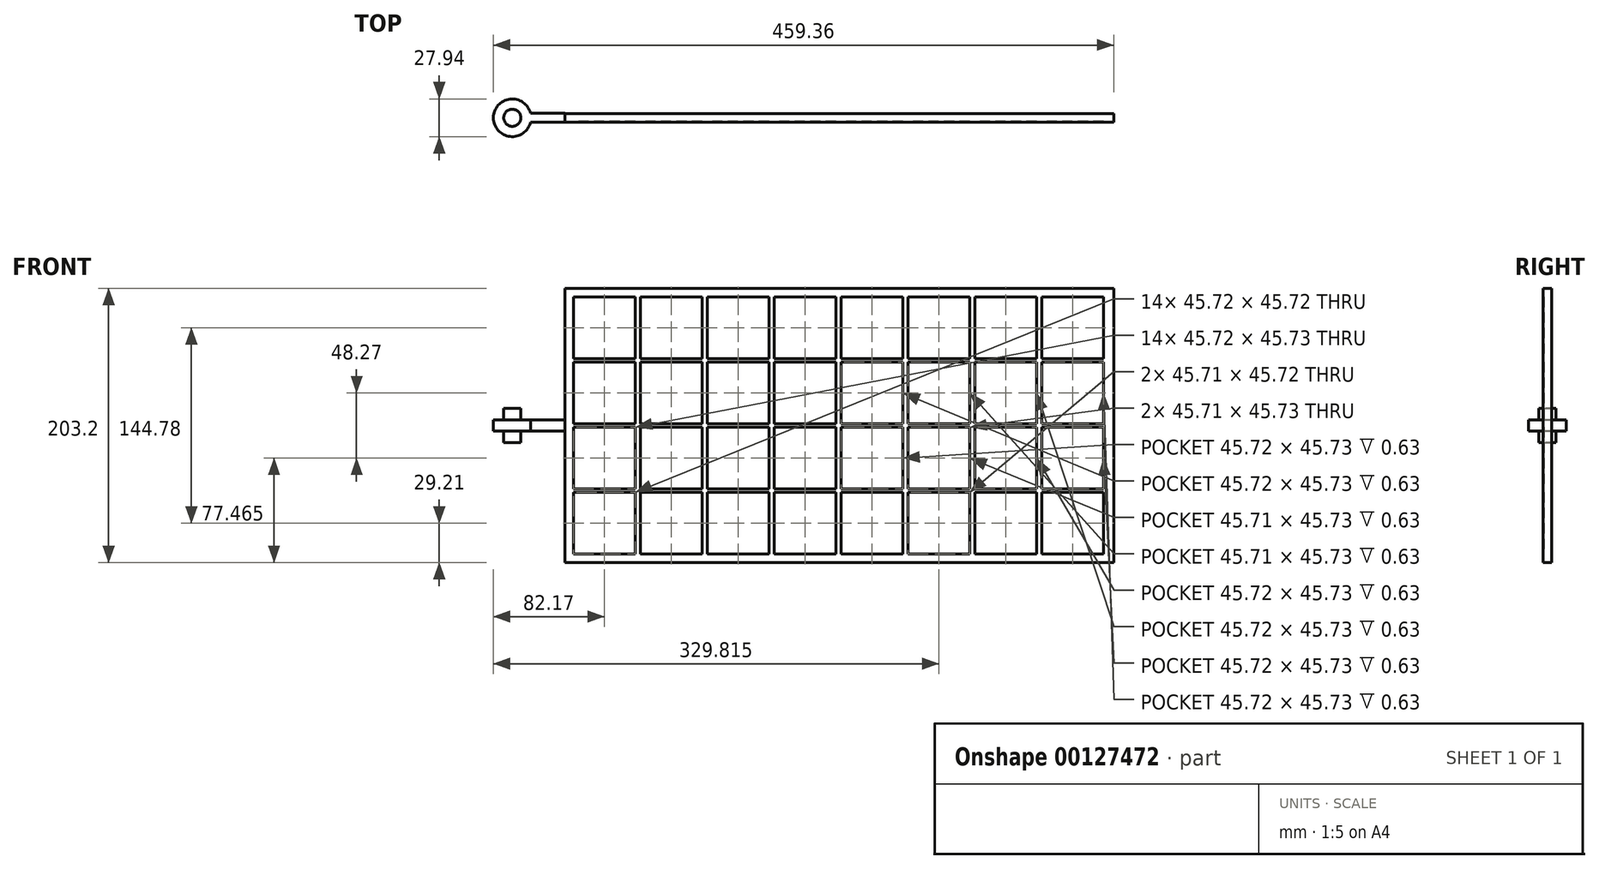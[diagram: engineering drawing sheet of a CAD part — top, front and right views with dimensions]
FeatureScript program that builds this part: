
annotation { "Feature Type Name" : "Feature", "Feature Type Description" : "" }
export const myFeature = defineFeature(function(context is Context, id is Id, definition is map)
    precondition{}
    {
        {
            var Q0;
            Q0=qCreatedBy(makeId("Top.planeOp"),FACE);
            var sketch = newSketch(context, id + "F0", { "sketchPlane" : qUnion([Q0])});
            skCircle(sketch, "E0", {"center": v(0, 0) * mm, "radius": 6.35 * mm});
            skSolve(sketch);
        }
        {
            var Q0;
            Q0 = qSketchRegion(id + "F0", true);
            extrude(context, id + "F1", {"entities" : qUnion([Q0]), "endBound" : BoundingType.SYMMETRIC, "depth" : 25.4 * mm});
        }
        {
            var Q0;
            Q0=qCreatedBy(makeId("Top.planeOp"),FACE);
            var sketch = newSketch(context, id + "F2", { "sketchPlane" : qUnion([Q0])});
            skArc(sketch, "E1", {"start": v(13.59, 3.26) * mm, "mid": v(-13.97, 0) * mm, "end": v(13.59, -3.26) * mm});
            skCircle(sketch, "E2.0", {"center": v(0, 0) * mm, "radius": 6.35 * mm});
            skLineSegment(sketch, "E3", {"start": v(13.59, 3.26) * mm, "end": v(38.99, 3.26) * mm});
            skLineSegment(sketch, "E4", {"start": v(0, 0) * mm, "end": v(2.18, 0) * mm});
            skLineSegment(sketch, "E5.MirrorCS", {"start": v(13.59, -3.26) * mm, "end": v(38.99, -3.26) * mm});
            skLineSegment(sketch, "E6", {"start": v(38.99, 3.26) * mm, "end": v(38.99, -3.26) * mm});
            skSolve(sketch);
        }
        {
            var Q0;
            Q0 = qSketchRegion(id + "F2", true);
            extrude(context, id + "F3", {"entities" : qUnion([Q0]), "operationType" : NewBodyOperationType.ADD, "endBound" : BoundingType.SYMMETRIC, "depth" : 8.38 * mm});
        }
        {
            var Q0;
            Q0=qCreatedBy(makeId("Front.planeOp"),FACE);
            var sketch = newSketch(context, id + "F4", { "sketchPlane" : qUnion([Q0])});
            skLineSegment(sketch, "E7.0", {"start": v(38.99, 4.2) * mm, "end": v(38.99, -4.2) * mm});
            skLineSegment(sketch, "E8", {"start": v(38.99, 0) * mm, "end": v(38.99, 101.6) * mm});
            skPoint(sketch, "E8.endSnap0", {"position": v(38.99, 0) * mm});
            skLineSegment(sketch, "E9", {"start": v(38.99, 0) * mm, "end": v(38.99, -101.6) * mm});
            skLineSegment(sketch, "E10", {"start": v(38.99, 101.6) * mm, "end": v(445.39, 101.6) * mm});
            skLineSegment(sketch, "E11.top", {"start": v(38.99, -101.6) * mm, "end": v(445.39, -101.6) * mm});
            skLineSegment(sketch, "E11.left", {"start": v(38.99, 101.6) * mm, "end": v(38.99, -101.6) * mm});
            skLineSegment(sketch, "E11.right", {"start": v(445.39, 101.6) * mm, "end": v(445.39, -101.6) * mm});
            skLineSegment(sketch, "E12.bottom", {"start": v(45.34, -95.25) * mm, "end": v(91.06, -95.25) * mm});
            skLineSegment(sketch, "E12.top", {"start": v(45.34, -49.53) * mm, "end": v(91.06, -49.53) * mm});
            skLineSegment(sketch, "E12.left", {"start": v(45.34, -95.25) * mm, "end": v(45.34, -49.53) * mm});
            skLineSegment(sketch, "E12.right", {"start": v(91.06, -95.25) * mm, "end": v(91.06, -49.53) * mm});
            skLineSegment(sketch, "E13.0.1.0", {"start": v(91.06, -47) * mm, "end": v(91.06, -1.27) * mm});
            skLineSegment(sketch, "E13.0.1.1", {"start": v(45.34, -47) * mm, "end": v(45.34, -1.27) * mm});
            skLineSegment(sketch, "E13.0.1.2", {"start": v(45.34, -1.27) * mm, "end": v(91.06, -1.27) * mm});
            skLineSegment(sketch, "E13.0.1.3", {"start": v(45.34, -47) * mm, "end": v(91.06, -47) * mm});
            skLineSegment(sketch, "E13.0.2.0", {"start": v(91.06, 1.27) * mm, "end": v(91.06, 47) * mm});
            skLineSegment(sketch, "E13.0.2.1", {"start": v(45.34, 1.27) * mm, "end": v(45.34, 47) * mm});
            skLineSegment(sketch, "E13.0.2.2", {"start": v(45.34, 47) * mm, "end": v(91.06, 47) * mm});
            skLineSegment(sketch, "E13.0.2.3", {"start": v(45.34, 1.27) * mm, "end": v(91.06, 1.27) * mm});
            skLineSegment(sketch, "E13.0.3.0", {"start": v(91.06, 49.53) * mm, "end": v(91.06, 95.25) * mm});
            skLineSegment(sketch, "E13.0.3.1", {"start": v(45.34, 49.53) * mm, "end": v(45.34, 95.25) * mm});
            skLineSegment(sketch, "E13.0.3.2", {"start": v(45.34, 95.25) * mm, "end": v(91.06, 95.25) * mm});
            skLineSegment(sketch, "E13.0.3.3", {"start": v(45.34, 49.53) * mm, "end": v(91.06, 49.53) * mm});
            skLineSegment(sketch, "E13.1.0.0", {"start": v(140.59, -95.25) * mm, "end": v(140.59, -49.53) * mm});
            skLineSegment(sketch, "E13.1.0.1", {"start": v(94.87, -95.25) * mm, "end": v(94.87, -49.53) * mm});
            skLineSegment(sketch, "E13.1.0.2", {"start": v(94.87, -49.53) * mm, "end": v(140.59, -49.53) * mm});
            skLineSegment(sketch, "E13.1.0.3", {"start": v(94.87, -95.25) * mm, "end": v(140.59, -95.25) * mm});
            skLineSegment(sketch, "E13.1.1.0", {"start": v(140.59, -47) * mm, "end": v(140.59, -1.27) * mm});
            skLineSegment(sketch, "E13.1.1.1", {"start": v(94.87, -47) * mm, "end": v(94.87, -1.27) * mm});
            skLineSegment(sketch, "E13.1.1.2", {"start": v(94.87, -1.27) * mm, "end": v(140.59, -1.27) * mm});
            skLineSegment(sketch, "E13.1.1.3", {"start": v(94.87, -47) * mm, "end": v(140.59, -47) * mm});
            skLineSegment(sketch, "E13.1.2.0", {"start": v(140.59, 1.27) * mm, "end": v(140.59, 47) * mm});
            skLineSegment(sketch, "E13.1.2.1", {"start": v(94.87, 1.27) * mm, "end": v(94.87, 47) * mm});
            skLineSegment(sketch, "E13.1.2.2", {"start": v(94.87, 47) * mm, "end": v(140.59, 47) * mm});
            skLineSegment(sketch, "E13.1.2.3", {"start": v(94.87, 1.27) * mm, "end": v(140.59, 1.27) * mm});
            skLineSegment(sketch, "E13.1.3.0", {"start": v(140.59, 49.53) * mm, "end": v(140.59, 95.25) * mm});
            skLineSegment(sketch, "E13.1.3.1", {"start": v(94.87, 49.53) * mm, "end": v(94.87, 95.25) * mm});
            skLineSegment(sketch, "E13.1.3.2", {"start": v(94.87, 95.25) * mm, "end": v(140.59, 95.25) * mm});
            skLineSegment(sketch, "E13.1.3.3", {"start": v(94.87, 49.53) * mm, "end": v(140.59, 49.53) * mm});
            skLineSegment(sketch, "E13.2.0.0", {"start": v(190.12, -95.25) * mm, "end": v(190.12, -49.53) * mm});
            skLineSegment(sketch, "E13.2.0.1", {"start": v(144.4, -95.25) * mm, "end": v(144.4, -49.53) * mm});
            skLineSegment(sketch, "E13.2.0.2", {"start": v(144.4, -49.53) * mm, "end": v(190.12, -49.53) * mm});
            skLineSegment(sketch, "E13.2.0.3", {"start": v(144.4, -95.25) * mm, "end": v(190.12, -95.25) * mm});
            skLineSegment(sketch, "E13.2.1.0", {"start": v(190.12, -47) * mm, "end": v(190.12, -1.27) * mm});
            skLineSegment(sketch, "E13.2.1.1", {"start": v(144.4, -47) * mm, "end": v(144.4, -1.27) * mm});
            skLineSegment(sketch, "E13.2.1.2", {"start": v(144.4, -1.27) * mm, "end": v(190.12, -1.27) * mm});
            skLineSegment(sketch, "E13.2.1.3", {"start": v(144.4, -47) * mm, "end": v(190.12, -47) * mm});
            skLineSegment(sketch, "E13.2.2.0", {"start": v(190.12, 1.27) * mm, "end": v(190.12, 47) * mm});
            skLineSegment(sketch, "E13.2.2.1", {"start": v(144.4, 1.27) * mm, "end": v(144.4, 47) * mm});
            skLineSegment(sketch, "E13.2.2.2", {"start": v(144.4, 47) * mm, "end": v(190.12, 47) * mm});
            skLineSegment(sketch, "E13.2.2.3", {"start": v(144.4, 1.27) * mm, "end": v(190.12, 1.27) * mm});
            skLineSegment(sketch, "E13.2.3.0", {"start": v(190.12, 49.53) * mm, "end": v(190.12, 95.25) * mm});
            skLineSegment(sketch, "E13.2.3.1", {"start": v(144.4, 49.53) * mm, "end": v(144.4, 95.25) * mm});
            skLineSegment(sketch, "E13.2.3.2", {"start": v(144.4, 95.25) * mm, "end": v(190.12, 95.25) * mm});
            skLineSegment(sketch, "E13.2.3.3", {"start": v(144.4, 49.53) * mm, "end": v(190.12, 49.53) * mm});
            skLineSegment(sketch, "E13.3.0.0", {"start": v(239.65, -95.25) * mm, "end": v(239.65, -49.53) * mm});
            skLineSegment(sketch, "E13.3.0.1", {"start": v(193.93, -95.25) * mm, "end": v(193.93, -49.53) * mm});
            skLineSegment(sketch, "E13.3.0.2", {"start": v(193.93, -49.53) * mm, "end": v(239.65, -49.53) * mm});
            skLineSegment(sketch, "E13.3.0.3", {"start": v(193.93, -95.25) * mm, "end": v(239.65, -95.25) * mm});
            skLineSegment(sketch, "E13.3.1.0", {"start": v(239.65, -47) * mm, "end": v(239.65, -1.27) * mm});
            skLineSegment(sketch, "E13.3.1.1", {"start": v(193.93, -47) * mm, "end": v(193.93, -1.27) * mm});
            skLineSegment(sketch, "E13.3.1.2", {"start": v(193.93, -1.27) * mm, "end": v(239.65, -1.27) * mm});
            skLineSegment(sketch, "E13.3.1.3", {"start": v(193.93, -47) * mm, "end": v(239.65, -47) * mm});
            skLineSegment(sketch, "E13.3.2.0", {"start": v(239.65, 1.27) * mm, "end": v(239.65, 47) * mm});
            skLineSegment(sketch, "E13.3.2.1", {"start": v(193.93, 1.27) * mm, "end": v(193.93, 47) * mm});
            skLineSegment(sketch, "E13.3.2.2", {"start": v(193.93, 47) * mm, "end": v(239.65, 47) * mm});
            skLineSegment(sketch, "E13.3.2.3", {"start": v(193.93, 1.27) * mm, "end": v(239.65, 1.27) * mm});
            skLineSegment(sketch, "E13.3.3.0", {"start": v(239.65, 49.53) * mm, "end": v(239.65, 95.25) * mm});
            skLineSegment(sketch, "E13.3.3.1", {"start": v(193.93, 49.53) * mm, "end": v(193.93, 95.25) * mm});
            skLineSegment(sketch, "E13.3.3.2", {"start": v(193.93, 95.25) * mm, "end": v(239.65, 95.25) * mm});
            skLineSegment(sketch, "E13.3.3.3", {"start": v(193.93, 49.53) * mm, "end": v(239.65, 49.53) * mm});
            skLineSegment(sketch, "E13.4.0.0", {"start": v(289.18, -95.25) * mm, "end": v(289.18, -49.53) * mm});
            skLineSegment(sketch, "E13.4.0.1", {"start": v(243.46, -95.25) * mm, "end": v(243.46, -49.53) * mm});
            skLineSegment(sketch, "E13.4.0.2", {"start": v(243.46, -49.53) * mm, "end": v(289.18, -49.53) * mm});
            skLineSegment(sketch, "E13.4.0.3", {"start": v(243.46, -95.25) * mm, "end": v(289.18, -95.25) * mm});
            skLineSegment(sketch, "E13.4.1.0", {"start": v(289.18, -47) * mm, "end": v(289.18, -1.27) * mm});
            skLineSegment(sketch, "E13.4.1.1", {"start": v(243.46, -47) * mm, "end": v(243.46, -1.27) * mm});
            skLineSegment(sketch, "E13.4.1.2", {"start": v(243.46, -1.27) * mm, "end": v(289.18, -1.27) * mm});
            skLineSegment(sketch, "E13.4.1.3", {"start": v(243.46, -47) * mm, "end": v(289.18, -47) * mm});
            skLineSegment(sketch, "E13.4.2.0", {"start": v(289.18, 1.27) * mm, "end": v(289.18, 47) * mm});
            skLineSegment(sketch, "E13.4.2.1", {"start": v(243.46, 1.27) * mm, "end": v(243.46, 47) * mm});
            skLineSegment(sketch, "E13.4.2.2", {"start": v(243.46, 47) * mm, "end": v(289.18, 47) * mm});
            skLineSegment(sketch, "E13.4.2.3", {"start": v(243.46, 1.27) * mm, "end": v(289.18, 1.27) * mm});
            skLineSegment(sketch, "E13.4.3.0", {"start": v(289.18, 49.53) * mm, "end": v(289.18, 95.25) * mm});
            skLineSegment(sketch, "E13.4.3.1", {"start": v(243.46, 49.53) * mm, "end": v(243.46, 95.25) * mm});
            skLineSegment(sketch, "E13.4.3.2", {"start": v(243.46, 95.25) * mm, "end": v(289.18, 95.25) * mm});
            skLineSegment(sketch, "E13.4.3.3", {"start": v(243.46, 49.53) * mm, "end": v(289.18, 49.53) * mm});
            skLineSegment(sketch, "E13.5.0.0", {"start": v(338.7, -95.25) * mm, "end": v(338.7, -49.53) * mm});
            skLineSegment(sketch, "E13.5.0.1", {"start": v(292.99, -95.25) * mm, "end": v(292.99, -49.53) * mm});
            skLineSegment(sketch, "E13.5.0.2", {"start": v(292.99, -49.53) * mm, "end": v(338.7, -49.53) * mm});
            skLineSegment(sketch, "E13.5.0.3", {"start": v(292.99, -95.25) * mm, "end": v(338.7, -95.25) * mm});
            skLineSegment(sketch, "E13.5.1.0", {"start": v(338.7, -47) * mm, "end": v(338.7, -1.27) * mm});
            skLineSegment(sketch, "E13.5.1.1", {"start": v(292.99, -47) * mm, "end": v(292.99, -1.27) * mm});
            skLineSegment(sketch, "E13.5.1.2", {"start": v(292.99, -1.27) * mm, "end": v(338.7, -1.27) * mm});
            skLineSegment(sketch, "E13.5.1.3", {"start": v(292.99, -47) * mm, "end": v(338.7, -47) * mm});
            skLineSegment(sketch, "E13.5.2.0", {"start": v(338.7, 1.27) * mm, "end": v(338.7, 47) * mm});
            skLineSegment(sketch, "E13.5.2.1", {"start": v(292.99, 1.27) * mm, "end": v(292.99, 47) * mm});
            skLineSegment(sketch, "E13.5.2.2", {"start": v(292.99, 47) * mm, "end": v(338.7, 47) * mm});
            skLineSegment(sketch, "E13.5.2.3", {"start": v(292.99, 1.27) * mm, "end": v(338.7, 1.27) * mm});
            skLineSegment(sketch, "E13.5.3.0", {"start": v(338.7, 49.53) * mm, "end": v(338.7, 95.25) * mm});
            skLineSegment(sketch, "E13.5.3.1", {"start": v(292.99, 49.53) * mm, "end": v(292.99, 95.25) * mm});
            skLineSegment(sketch, "E13.5.3.2", {"start": v(292.99, 95.25) * mm, "end": v(338.7, 95.25) * mm});
            skLineSegment(sketch, "E13.5.3.3", {"start": v(292.99, 49.53) * mm, "end": v(338.7, 49.53) * mm});
            skLineSegment(sketch, "E13.6.0.0", {"start": v(388.24, -95.25) * mm, "end": v(388.24, -49.53) * mm});
            skLineSegment(sketch, "E13.6.0.1", {"start": v(342.52, -95.25) * mm, "end": v(342.52, -49.53) * mm});
            skLineSegment(sketch, "E13.6.0.2", {"start": v(342.52, -49.53) * mm, "end": v(388.24, -49.53) * mm});
            skLineSegment(sketch, "E13.6.0.3", {"start": v(342.52, -95.25) * mm, "end": v(388.24, -95.25) * mm});
            skLineSegment(sketch, "E13.6.1.0", {"start": v(388.24, -47) * mm, "end": v(388.24, -1.27) * mm});
            skLineSegment(sketch, "E13.6.1.1", {"start": v(342.52, -47) * mm, "end": v(342.52, -1.27) * mm});
            skLineSegment(sketch, "E13.6.1.2", {"start": v(342.52, -1.27) * mm, "end": v(388.24, -1.27) * mm});
            skLineSegment(sketch, "E13.6.1.3", {"start": v(342.52, -47) * mm, "end": v(388.24, -47) * mm});
            skLineSegment(sketch, "E13.6.2.0", {"start": v(388.24, 1.27) * mm, "end": v(388.24, 47) * mm});
            skLineSegment(sketch, "E13.6.2.1", {"start": v(342.52, 1.27) * mm, "end": v(342.52, 47) * mm});
            skLineSegment(sketch, "E13.6.2.2", {"start": v(342.52, 47) * mm, "end": v(388.24, 47) * mm});
            skLineSegment(sketch, "E13.6.2.3", {"start": v(342.52, 1.27) * mm, "end": v(388.24, 1.27) * mm});
            skLineSegment(sketch, "E13.6.3.0", {"start": v(388.24, 49.53) * mm, "end": v(388.24, 95.25) * mm});
            skLineSegment(sketch, "E13.6.3.1", {"start": v(342.52, 49.53) * mm, "end": v(342.52, 95.25) * mm});
            skLineSegment(sketch, "E13.6.3.2", {"start": v(342.52, 95.25) * mm, "end": v(388.24, 95.25) * mm});
            skLineSegment(sketch, "E13.6.3.3", {"start": v(342.52, 49.53) * mm, "end": v(388.24, 49.53) * mm});
            skLineSegment(sketch, "E13.7.0.0", {"start": v(437.77, -95.25) * mm, "end": v(437.77, -49.53) * mm});
            skLineSegment(sketch, "E13.7.0.1", {"start": v(392.05, -95.25) * mm, "end": v(392.05, -49.53) * mm});
            skLineSegment(sketch, "E13.7.0.2", {"start": v(392.05, -49.53) * mm, "end": v(437.77, -49.53) * mm});
            skLineSegment(sketch, "E13.7.0.3", {"start": v(392.05, -95.25) * mm, "end": v(437.77, -95.25) * mm});
            skLineSegment(sketch, "E13.7.1.0", {"start": v(437.77, -47) * mm, "end": v(437.77, -1.27) * mm});
            skLineSegment(sketch, "E13.7.1.1", {"start": v(392.05, -47) * mm, "end": v(392.05, -1.27) * mm});
            skLineSegment(sketch, "E13.7.1.2", {"start": v(392.05, -1.27) * mm, "end": v(437.77, -1.27) * mm});
            skLineSegment(sketch, "E13.7.1.3", {"start": v(392.05, -47) * mm, "end": v(437.77, -47) * mm});
            skLineSegment(sketch, "E13.7.2.0", {"start": v(437.77, 1.27) * mm, "end": v(437.77, 47) * mm});
            skLineSegment(sketch, "E13.7.2.1", {"start": v(392.05, 1.27) * mm, "end": v(392.05, 47) * mm});
            skLineSegment(sketch, "E13.7.2.2", {"start": v(392.05, 47) * mm, "end": v(437.77, 47) * mm});
            skLineSegment(sketch, "E13.7.2.3", {"start": v(392.05, 1.27) * mm, "end": v(437.77, 1.27) * mm});
            skLineSegment(sketch, "E13.7.3.0", {"start": v(437.77, 49.53) * mm, "end": v(437.77, 95.25) * mm});
            skLineSegment(sketch, "E13.7.3.1", {"start": v(392.05, 49.53) * mm, "end": v(392.05, 95.25) * mm});
            skLineSegment(sketch, "E13.7.3.2", {"start": v(392.05, 95.25) * mm, "end": v(437.77, 95.25) * mm});
            skLineSegment(sketch, "E13.7.3.3", {"start": v(392.05, 49.53) * mm, "end": v(437.77, 49.53) * mm});
            skLineSegment(sketch, "E13.direction1", {"start": v(45.34, -95.25) * mm, "end": v(94.87, -95.25) * mm, "construction": true});
            skLineSegment(sketch, "E13.direction2", {"start": v(45.34, -95.25) * mm, "end": v(45.34, -47) * mm, "construction": true});
            skSolve(sketch);
        }
        {
            var Q0;
            Q0 = qSketchRegion(id + "F4", true);
            extrude(context, id + "F5", {"entities" : qUnion([Q0]), "operationType" : NewBodyOperationType.ADD, "oppositeDirection" : true, "depth" : 3.17 * mm});
        }
        {
            var Q0;
            Q0=makeQuery(id+"F5.opExtrude","CAP_FACE",FACE,{"disambiguationData":[OSD([sQuery(id+"F4.wireOp",EDGE,"E10"),sQuery(id+"F4.wireOp",EDGE,"E11.top"),sQuery(id+"F4.wireOp",EDGE,"E11.left"),sQuery(id+"F4.wireOp",EDGE,"E11.right"),sQuery(id+"F4.wireOp",EDGE,"E12.bottom"),sQuery(id+"F4.wireOp",EDGE,"E12.top"),sQuery(id+"F4.wireOp",EDGE,"E12.left"),sQuery(id+"F4.wireOp",EDGE,"E12.right"),sQuery(id+"F4.wireOp",EDGE,"E13.0.1.0"),sQuery(id+"F4.wireOp",EDGE,"E13.0.1.1"),sQuery(id+"F4.wireOp",EDGE,"E13.0.1.2"),sQuery(id+"F4.wireOp",EDGE,"E13.0.1.3"),sQuery(id+"F4.wireOp",EDGE,"E13.0.2.0"),sQuery(id+"F4.wireOp",EDGE,"E13.0.2.1"),sQuery(id+"F4.wireOp",EDGE,"E13.0.2.2"),sQuery(id+"F4.wireOp",EDGE,"E13.0.2.3"),sQuery(id+"F4.wireOp",EDGE,"E13.0.3.0"),sQuery(id+"F4.wireOp",EDGE,"E13.0.3.1"),sQuery(id+"F4.wireOp",EDGE,"E13.0.3.2"),sQuery(id+"F4.wireOp",EDGE,"E13.0.3.3"),sQuery(id+"F4.wireOp",EDGE,"E13.1.0.0"),sQuery(id+"F4.wireOp",EDGE,"E13.1.0.1"),sQuery(id+"F4.wireOp",EDGE,"E13.1.0.2"),sQuery(id+"F4.wireOp",EDGE,"E13.1.0.3"),sQuery(id+"F4.wireOp",EDGE,"E13.1.1.0"),sQuery(id+"F4.wireOp",EDGE,"E13.1.1.1"),sQuery(id+"F4.wireOp",EDGE,"E13.1.1.2"),sQuery(id+"F4.wireOp",EDGE,"E13.1.1.3"),sQuery(id+"F4.wireOp",EDGE,"E13.1.2.0"),sQuery(id+"F4.wireOp",EDGE,"E13.1.2.1"),sQuery(id+"F4.wireOp",EDGE,"E13.1.2.2"),sQuery(id+"F4.wireOp",EDGE,"E13.1.2.3"),sQuery(id+"F4.wireOp",EDGE,"E13.1.3.0"),sQuery(id+"F4.wireOp",EDGE,"E13.1.3.1"),sQuery(id+"F4.wireOp",EDGE,"E13.1.3.2"),sQuery(id+"F4.wireOp",EDGE,"E13.1.3.3"),sQuery(id+"F4.wireOp",EDGE,"E13.2.0.0"),sQuery(id+"F4.wireOp",EDGE,"E13.2.0.1"),sQuery(id+"F4.wireOp",EDGE,"E13.2.0.2"),sQuery(id+"F4.wireOp",EDGE,"E13.2.0.3"),sQuery(id+"F4.wireOp",EDGE,"E13.2.1.0"),sQuery(id+"F4.wireOp",EDGE,"E13.2.1.1"),sQuery(id+"F4.wireOp",EDGE,"E13.2.1.2"),sQuery(id+"F4.wireOp",EDGE,"E13.2.1.3"),sQuery(id+"F4.wireOp",EDGE,"E13.2.2.0"),sQuery(id+"F4.wireOp",EDGE,"E13.2.2.1"),sQuery(id+"F4.wireOp",EDGE,"E13.2.2.2"),sQuery(id+"F4.wireOp",EDGE,"E13.2.2.3"),sQuery(id+"F4.wireOp",EDGE,"E13.2.3.0"),sQuery(id+"F4.wireOp",EDGE,"E13.2.3.1"),sQuery(id+"F4.wireOp",EDGE,"E13.2.3.2"),sQuery(id+"F4.wireOp",EDGE,"E13.2.3.3"),sQuery(id+"F4.wireOp",EDGE,"E13.3.0.0"),sQuery(id+"F4.wireOp",EDGE,"E13.3.0.1"),sQuery(id+"F4.wireOp",EDGE,"E13.3.0.2"),sQuery(id+"F4.wireOp",EDGE,"E13.3.0.3"),sQuery(id+"F4.wireOp",EDGE,"E13.3.1.0"),sQuery(id+"F4.wireOp",EDGE,"E13.3.1.1"),sQuery(id+"F4.wireOp",EDGE,"E13.3.1.2"),sQuery(id+"F4.wireOp",EDGE,"E13.3.1.3"),sQuery(id+"F4.wireOp",EDGE,"E13.3.2.0"),sQuery(id+"F4.wireOp",EDGE,"E13.3.2.1"),sQuery(id+"F4.wireOp",EDGE,"E13.3.2.2"),sQuery(id+"F4.wireOp",EDGE,"E13.3.2.3"),sQuery(id+"F4.wireOp",EDGE,"E13.3.3.0"),sQuery(id+"F4.wireOp",EDGE,"E13.3.3.1"),sQuery(id+"F4.wireOp",EDGE,"E13.3.3.2"),sQuery(id+"F4.wireOp",EDGE,"E13.3.3.3"),sQuery(id+"F4.wireOp",EDGE,"E13.4.0.0"),sQuery(id+"F4.wireOp",EDGE,"E13.4.0.1"),sQuery(id+"F4.wireOp",EDGE,"E13.4.0.2"),sQuery(id+"F4.wireOp",EDGE,"E13.4.0.3"),sQuery(id+"F4.wireOp",EDGE,"E13.4.1.0"),sQuery(id+"F4.wireOp",EDGE,"E13.4.1.1"),sQuery(id+"F4.wireOp",EDGE,"E13.4.1.2"),sQuery(id+"F4.wireOp",EDGE,"E13.4.1.3"),sQuery(id+"F4.wireOp",EDGE,"E13.4.2.0"),sQuery(id+"F4.wireOp",EDGE,"E13.4.2.1"),sQuery(id+"F4.wireOp",EDGE,"E13.4.2.2"),sQuery(id+"F4.wireOp",EDGE,"E13.4.2.3"),sQuery(id+"F4.wireOp",EDGE,"E13.4.3.0"),sQuery(id+"F4.wireOp",EDGE,"E13.4.3.1"),sQuery(id+"F4.wireOp",EDGE,"E13.4.3.2"),sQuery(id+"F4.wireOp",EDGE,"E13.4.3.3"),sQuery(id+"F4.wireOp",EDGE,"E13.5.0.0"),sQuery(id+"F4.wireOp",EDGE,"E13.5.0.1"),sQuery(id+"F4.wireOp",EDGE,"E13.5.0.2"),sQuery(id+"F4.wireOp",EDGE,"E13.5.0.3"),sQuery(id+"F4.wireOp",EDGE,"E13.5.1.0"),sQuery(id+"F4.wireOp",EDGE,"E13.5.1.1"),sQuery(id+"F4.wireOp",EDGE,"E13.5.1.2"),sQuery(id+"F4.wireOp",EDGE,"E13.5.1.3"),sQuery(id+"F4.wireOp",EDGE,"E13.5.2.0"),sQuery(id+"F4.wireOp",EDGE,"E13.5.2.1"),sQuery(id+"F4.wireOp",EDGE,"E13.5.2.2"),sQuery(id+"F4.wireOp",EDGE,"E13.5.2.3"),sQuery(id+"F4.wireOp",EDGE,"E13.5.3.0"),sQuery(id+"F4.wireOp",EDGE,"E13.5.3.1"),sQuery(id+"F4.wireOp",EDGE,"E13.5.3.2"),sQuery(id+"F4.wireOp",EDGE,"E13.5.3.3"),sQuery(id+"F4.wireOp",EDGE,"E13.6.0.0"),sQuery(id+"F4.wireOp",EDGE,"E13.6.0.1"),sQuery(id+"F4.wireOp",EDGE,"E13.6.0.2"),sQuery(id+"F4.wireOp",EDGE,"E13.6.0.3"),sQuery(id+"F4.wireOp",EDGE,"E13.6.1.0"),sQuery(id+"F4.wireOp",EDGE,"E13.6.1.1"),sQuery(id+"F4.wireOp",EDGE,"E13.6.1.2"),sQuery(id+"F4.wireOp",EDGE,"E13.6.1.3"),sQuery(id+"F4.wireOp",EDGE,"E13.6.2.0"),sQuery(id+"F4.wireOp",EDGE,"E13.6.2.1"),sQuery(id+"F4.wireOp",EDGE,"E13.6.2.2"),sQuery(id+"F4.wireOp",EDGE,"E13.6.2.3"),sQuery(id+"F4.wireOp",EDGE,"E13.6.3.0"),sQuery(id+"F4.wireOp",EDGE,"E13.6.3.1"),sQuery(id+"F4.wireOp",EDGE,"E13.6.3.2"),sQuery(id+"F4.wireOp",EDGE,"E13.6.3.3"),sQuery(id+"F4.wireOp",EDGE,"E13.7.0.0"),sQuery(id+"F4.wireOp",EDGE,"E13.7.0.1"),sQuery(id+"F4.wireOp",EDGE,"E13.7.0.2"),sQuery(id+"F4.wireOp",EDGE,"E13.7.0.3"),sQuery(id+"F4.wireOp",EDGE,"E13.7.1.0"),sQuery(id+"F4.wireOp",EDGE,"E13.7.1.1"),sQuery(id+"F4.wireOp",EDGE,"E13.7.1.2"),sQuery(id+"F4.wireOp",EDGE,"E13.7.1.3"),sQuery(id+"F4.wireOp",EDGE,"E13.7.2.0"),sQuery(id+"F4.wireOp",EDGE,"E13.7.2.1"),sQuery(id+"F4.wireOp",EDGE,"E13.7.2.2"),sQuery(id+"F4.wireOp",EDGE,"E13.7.2.3"),sQuery(id+"F4.wireOp",EDGE,"E13.7.3.0"),sQuery(id+"F4.wireOp",EDGE,"E13.7.3.1"),sQuery(id+"F4.wireOp",EDGE,"E13.7.3.2"),sQuery(id+"F4.wireOp",EDGE,"E13.7.3.3")])],"isStart":true});
            var sketch = newSketch(context, id + "F6", { "sketchPlane" : qUnion([Q0])});
            skSolve(sketch);
        }
        {
            var Q0;
            {var subQ72=sQuery(id+"F4.wireOp",EDGE,"E10");Q0=makeQuery(id+"F6.imprint","IMPRINT",FACE,{"disambiguationData":[TD([[makeQuery(id+"F6.imprint","IMPRINT",EDGE,{"derivedFrom":makeQuery(id+"F5.opExtrude","CAP_EDGE",EDGE,{"disambiguationData":[OSD([subQ72])],"isStart":true})}),-1.0]])]});}
            var sketch = newSketch(context, id + "F7", { "sketchPlane" : qUnion([Q0])});
            skLineSegment(sketch, "E14.bottom", {"start": v(41.78, 98.8) * mm, "end": v(441.83, 98.8) * mm});
            skLineSegment(sketch, "E14.top", {"start": v(41.78, -98.04) * mm, "end": v(441.83, -98.04) * mm});
            skLineSegment(sketch, "E14.left", {"start": v(41.78, 98.8) * mm, "end": v(41.78, -98.04) * mm});
            skLineSegment(sketch, "E14.right", {"start": v(441.83, 98.8) * mm, "end": v(441.83, -98.04) * mm});
            skLineSegment(sketch, "E15.0", {"start": v(45.34, 49.53) * mm, "end": v(45.34, 95.25) * mm});
            skLineSegment(sketch, "E15.1", {"start": v(45.34, 95.25) * mm, "end": v(91.06, 95.25) * mm});
            skLineSegment(sketch, "E16.0", {"start": v(437.77, -95.25) * mm, "end": v(437.77, -49.53) * mm});
            skLineSegment(sketch, "E16.1", {"start": v(392.05, -95.25) * mm, "end": v(437.77, -95.25) * mm});
            skSolve(sketch);
        }
        {
            var Q0;
            Q0 = qSketchRegion(id + "F7", true);
            extrude(context, id + "F8", {"entities" : qUnion([Q0]), "operationType" : NewBodyOperationType.REMOVE, "oppositeDirection" : true, "depth" : 2.54 * mm});
        }
        {
            var Q0;
            Q0=makeQuery(id+"F6.imprint","IMPRINT",FACE,{"disambiguationData":[TD([[makeQuery(id+"F6.imprint","IMPRINT",EDGE,{"derivedFrom":makeQuery(id+"F5.opExtrude","CAP_EDGE",EDGE,{"disambiguationData":[OSD([sQuery(id+"F4.wireOp",EDGE,"E13.2.3.0")])],"isStart":true})}),1.0]])]});
            cPlane(context, id + "F9", {"entities" : qUnion([Q0]), "cplaneType" : CPlaneType.OFFSET, "offset" : 2.54 * mm, "oppositeDirection" : true, "width" : 152.4 * mm, "height" : 152.4 * mm});
        }
        {
            var Q0;
            Q0=qCreatedBy(id+"F9.planeOp",FACE);
            var sketch = newSketch(context, id + "F10", { "sketchPlane" : qUnion([Q0])});
            skLineSegment(sketch, "E17.0", {"start": v(41.78, 98.8) * mm, "end": v(41.78, -98.04) * mm});
            skLineSegment(sketch, "E18.0", {"start": v(41.78, 98.8) * mm, "end": v(441.83, 98.8) * mm});
            skLineSegment(sketch, "E19.0", {"start": v(441.83, 98.8) * mm, "end": v(441.83, -98.04) * mm});
            skLineSegment(sketch, "E20.0", {"start": v(41.78, -98.04) * mm, "end": v(441.83, -98.04) * mm});
            skSolve(sketch);
        }
        {
            var Q0;
            Q0 = qSketchRegion(id + "F10", true);
            extrude(context, id + "F11", {"entities" : qUnion([Q0]), "depth" : 5.08 * mm});
        }
        {
            var Q0;
            Q0=makeQuery(id+"F1.opExtrude","SWEPT_BODY",BODY,{"disambiguationData":[OSD([sQuery(id+"F0.wireOp",EDGE,"E0")])]});
            var Q1;
            {var subQ72=sQuery(id+"F4.wireOp",EDGE,"E10");Q1=makeQuery(id+"F6.imprint","IMPRINT",FACE,{"disambiguationData":[TD([[makeQuery(id+"F6.imprint","IMPRINT",EDGE,{"derivedFrom":makeQuery(id+"F5.opExtrude","CAP_EDGE",EDGE,{"disambiguationData":[OSD([subQ72])],"isStart":true})}),-1.0]])]});}
            mirror(context, id + "F12", {"operationType" : NewBodyOperationType.ADD, "entities" : qUnion([Q0]), "mirrorPlane" : qUnion([Q1])});
        }
    });
